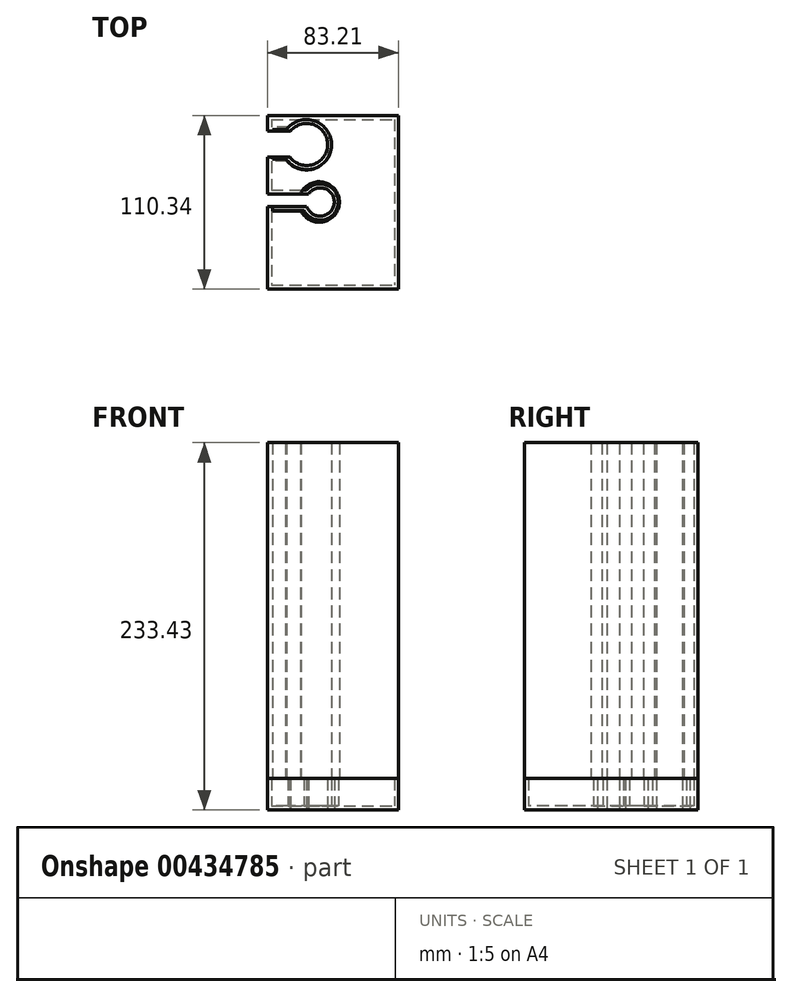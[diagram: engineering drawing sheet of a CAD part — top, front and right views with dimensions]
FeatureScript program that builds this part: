
annotation { "Feature Type Name" : "Feature", "Feature Type Description" : "" }
export const myFeature = defineFeature(function(context is Context, id is Id, definition is map)
    precondition{}
    {
        {
            var Q0;
            Q0=qCreatedBy(makeId("Top.planeOp"),FACE);
            var sketch = newSketch(context, id + "F0", { "sketchPlane" : qUnion([Q0])});
            skLineSegment(sketch, "E0.bottom", {"start": v(-47.24, 55.02) * mm, "end": v(35.97, 55.02) * mm});
            skLineSegment(sketch, "E0.top", {"start": v(-47.24, -55.32) * mm, "end": v(35.97, -55.32) * mm});
            skLineSegment(sketch, "E0.left", {"start": v(-47.24, 55.02) * mm, "end": v(-47.24, -55.32) * mm});
            skLineSegment(sketch, "E0.right", {"start": v(35.97, 55.02) * mm, "end": v(35.97, -55.32) * mm});
            skCircle(sketch, "E1", {"center": v(-22.3, 36.55) * mm, "radius": 13.37 * mm});
            skLineSegment(sketch, "E2.bottom", {"start": v(-32.56, 45.13) * mm, "end": v(-47.24, 45.13) * mm});
            skLineSegment(sketch, "E2.top", {"start": v(-32.56, 28.5) * mm, "end": v(-47.24, 28.5) * mm});
            skLineSegment(sketch, "E2.left", {"start": v(-32.56, 45.13) * mm, "end": v(-32.56, 28.5) * mm});
            skLineSegment(sketch, "E2.right", {"start": v(-47.24, 45.13) * mm, "end": v(-47.24, 28.5) * mm});
            skLineSegment(sketch, "E3.bottom", {"start": v(-47.24, 5.03) * mm, "end": v(-20.73, 5.03) * mm});
            skLineSegment(sketch, "E3.top", {"start": v(-47.24, -2.9) * mm, "end": v(-20.73, -2.9) * mm});
            skLineSegment(sketch, "E3.left", {"start": v(-47.24, 5.03) * mm, "end": v(-47.24, -2.9) * mm});
            skLineSegment(sketch, "E3.right", {"start": v(-20.73, 5.03) * mm, "end": v(-20.73, -2.9) * mm});
            skCircle(sketch, "E4", {"center": v(-13.72, 0) * mm, "radius": 9 * mm});
            skSolve(sketch);
        }
        {
            var Q0;
            {var subQ5=sQuery(id+"F0.wireOp",EDGE,"E0.bottom");Q0=makeQuery(id+"F0.imprint","IMPRINT",FACE,{"disambiguationData":[TD([[makeQuery(id+"F0.imprint","IMPRINT",EDGE,{"derivedFrom":subQ5}),-1.0]])]});}
            extrude(context, id + "F1", {"entities" : qUnion([Q0]), "depth" : 20.07 * mm});
        }
        {
            var Q0;
            Q0=makeQuery(id+"F1.opExtrude","CAP_FACE",FACE,{"disambiguationData":[OSD([sQuery(id+"F0.wireOp",EDGE,"E0.bottom"),sQuery(id+"F0.wireOp",EDGE,"E0.top"),sQuery(id+"F0.wireOp",EDGE,"E0.left"),sQuery(id+"F0.wireOp",EDGE,"E0.right"),sQuery(id+"F0.wireOp",EDGE,"E1"),sQuery(id+"F0.wireOp",EDGE,"E2.bottom"),sQuery(id+"F0.wireOp",EDGE,"E2.top")])],"isStart":false});
            var sketch = newSketch(context, id + "F2", { "sketchPlane" : qUnion([Q0])});
            skSolve(sketch);
        }
        {
            var Q0;
            Q0=makeQuery(id+"F1.opExtrude","CAP_FACE",FACE,{"disambiguationData":[OSD([sQuery(id+"F0.wireOp",EDGE,"E0.bottom"),sQuery(id+"F0.wireOp",EDGE,"E0.top"),sQuery(id+"F0.wireOp",EDGE,"E0.left"),sQuery(id+"F0.wireOp",EDGE,"E0.right"),sQuery(id+"F0.wireOp",EDGE,"E1"),sQuery(id+"F0.wireOp",EDGE,"E2.bottom"),sQuery(id+"F0.wireOp",EDGE,"E2.top"),sQuery(id+"F0.wireOp",EDGE,"E3.bottom"),sQuery(id+"F0.wireOp",EDGE,"E3.top"),sQuery(id+"F0.wireOp",EDGE,"E4")])],"isStart":false});
            shell(context, id + "F3", {"entities" : qUnion([Q0]), "thickness" : 2.54 * mm});
        }
        {
            var Q0;
            {var subQ7=sQuery(id+"F0.wireOp",EDGE,"E0.bottom");Q0=makeQuery(id+"F2.imprint","IMPRINT",FACE,{"disambiguationData":[TD([[makeQuery(id+"F2.imprint","IMPRINT",EDGE,{"derivedFrom":makeQuery(id+"F1.opExtrude","CAP_EDGE",EDGE,{"disambiguationData":[OSD([subQ7])],"isStart":false})}),-1.0]])]});}
            var sketch = newSketch(context, id + "F4", { "sketchPlane" : qUnion([Q0])});
            skCircle(sketch, "E5", {"center": v(-22.45, 36.38) * mm, "radius": 15.97 * mm});
            skCircle(sketch, "E6", {"center": v(-14.36, 0) * mm, "radius": 12.86 * mm});
            skLineSegment(sketch, "E7.bottom", {"start": v(-33.26, 46.1) * mm, "end": v(-44.1, 46.1) * mm});
            skLineSegment(sketch, "E7.top", {"start": v(-33.26, 27.36) * mm, "end": v(-44.1, 27.36) * mm});
            skLineSegment(sketch, "E7.left", {"start": v(-33.26, 46.1) * mm, "end": v(-33.26, 27.36) * mm});
            skLineSegment(sketch, "E7.right", {"start": v(-44.1, 46.1) * mm, "end": v(-44.1, 27.36) * mm});
            skLineSegment(sketch, "E8.bottom", {"start": v(-22.97, 4.39) * mm, "end": v(-44.1, 4.39) * mm});
            skLineSegment(sketch, "E8.top", {"start": v(-22.97, -5.89) * mm, "end": v(-44.1, -5.89) * mm});
            skLineSegment(sketch, "E8.left", {"start": v(-22.97, 4.39) * mm, "end": v(-22.97, -5.89) * mm});
            skLineSegment(sketch, "E8.right", {"start": v(-44.1, 4.39) * mm, "end": v(-44.1, -5.89) * mm});
            skSolve(sketch);
        }
        {
            var Q0;
            {var subQ18=sQuery(id+"F0.wireOp",EDGE,"E0.bottom");Q0=makeQuery(id+"F4.imprint","IMPRINT",FACE,{"disambiguationData":[TD([[makeQuery(id+"F4.imprint","IMPRINT",EDGE,{"derivedFrom":makeQuery(id+"F2.imprint","IMPRINT",EDGE,{"derivedFrom":makeQuery(id+"F1.opExtrude","CAP_EDGE",EDGE,{"disambiguationData":[OSD([subQ18])],"isStart":false})})}),-1.0]])]});}
            extrude(context, id + "F5", {"entities" : qUnion([Q0]), "depth" : 213.36 * mm});
        }
    });
